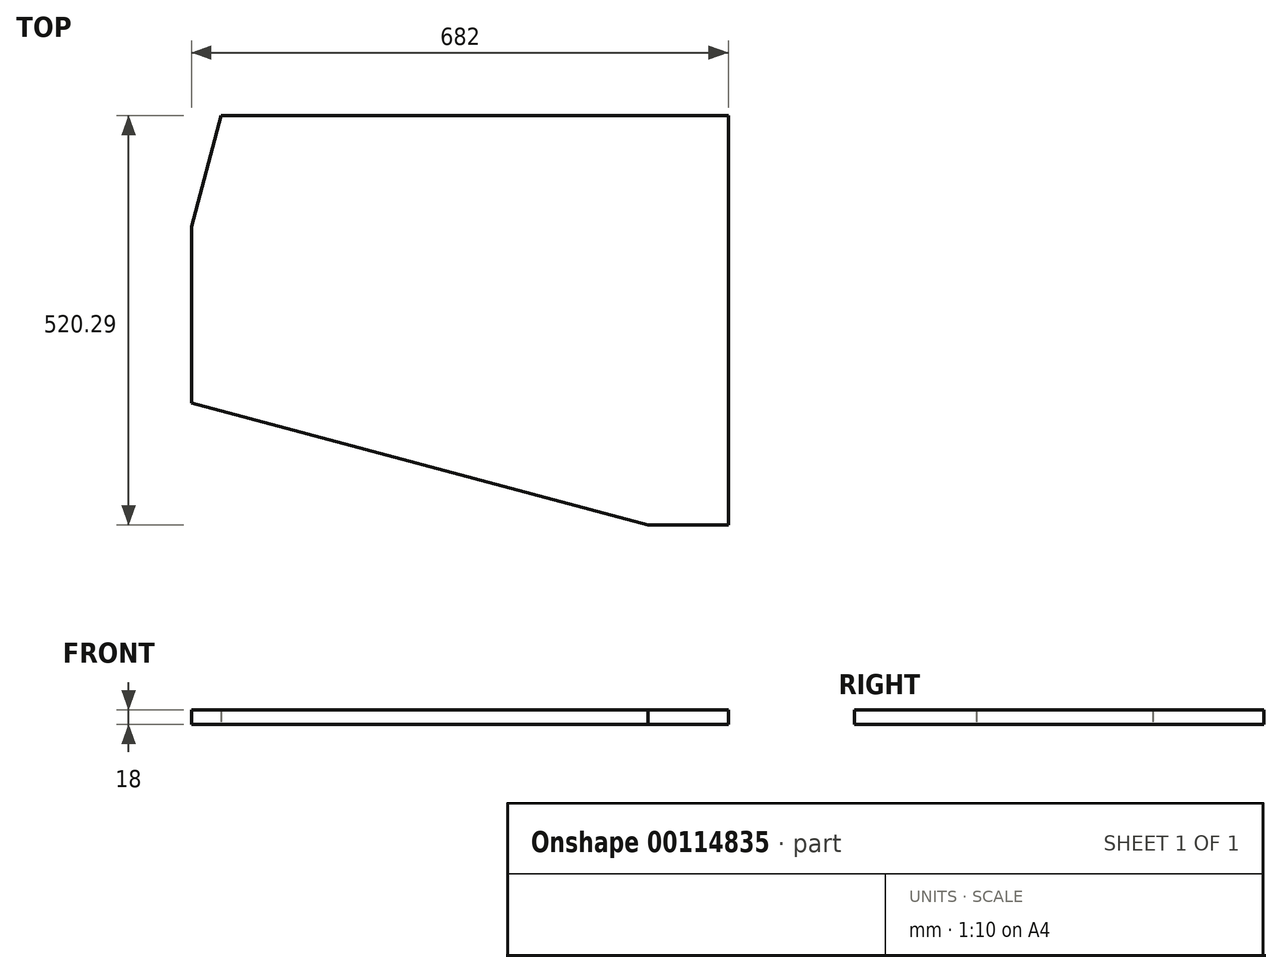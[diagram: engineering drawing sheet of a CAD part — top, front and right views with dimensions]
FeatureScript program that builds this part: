
annotation { "Feature Type Name" : "Feature", "Feature Type Description" : "" }
export const myFeature = defineFeature(function(context is Context, id is Id, definition is map)
    precondition{}
    {
        {
            var Q0;
            Q0=qCreatedBy(makeId("Top.planeOp"),FACE);
            var sketch = newSketch(context, id + "F0", { "sketchPlane" : qUnion([Q0])});
            skLineSegment(sketch, "E0.bottom", {"start": v(-1129.95, 340.55) * mm, "end": v(-447.95, 340.55) * mm, "construction": true});
            skLineSegment(sketch, "E0.top", {"start": v(-1129.95, -24.45) * mm, "end": v(-447.95, -24.45) * mm, "construction": true});
            skLineSegment(sketch, "E0.left", {"start": v(-1129.95, 340.55) * mm, "end": v(-1129.95, -24.45) * mm, "construction": true});
            skLineSegment(sketch, "E0.right", {"start": v(-447.95, 340.55) * mm, "end": v(-447.95, 100.55) * mm});
            skLineSegment(sketch, "E1", {"start": v(-1129.95, -24.45) * mm, "end": v(-1032.15, 340.55) * mm, "construction": true});
            skLineSegment(sketch, "E2", {"start": v(-447.95, -24.45) * mm, "end": v(-447.95, -179.74) * mm});
            skLineSegment(sketch, "E3", {"start": v(-447.95, 340.55) * mm, "end": v(-301.18, 340.55) * mm, "construction": true});
            skLineSegment(sketch, "E4", {"start": v(-301.18, 340.55) * mm, "end": v(-440.6, -179.74) * mm, "construction": true});
            skLineSegment(sketch, "E5", {"start": v(-1129.95, 340.55) * mm, "end": v(-1221.2, 0) * mm, "construction": true});
            skLineSegment(sketch, "E6", {"start": v(-1221.2, 0) * mm, "end": v(-1129.95, -24.45) * mm, "construction": true});
            skLineSegment(sketch, "E7", {"start": v(-1129.95, 340.55) * mm, "end": v(-1084.26, 511.05) * mm, "construction": true});
            skLineSegment(sketch, "E8", {"start": v(-447.95, 340.55) * mm, "end": v(-1084.26, 511.05) * mm, "construction": true});
            skLineSegment(sketch, "E9", {"start": v(-447.95, 340.55) * mm, "end": v(-311.02, 303.86) * mm, "construction": true});
            skPoint(sketch, "E10", {"position": v(-1048.98, 501.6) * mm});
            skLineSegment(sketch, "E11", {"start": v(-1048.98, 501.6) * mm, "end": v(-1185.92, -9.45) * mm, "construction": true});
            skPoint(sketch, "E12", {"position": v(-1092.14, 340.55) * mm});
            skPoint(sketch, "E13", {"position": v(-1129.95, 199.43) * mm});
            skLineSegment(sketch, "E14", {"start": v(-1129.95, -24.45) * mm, "end": v(-1129.95, 199.43) * mm});
            skLineSegment(sketch, "E15", {"start": v(-1092.14, 340.55) * mm, "end": v(-447.95, 340.55) * mm});
            skLineSegment(sketch, "E16", {"start": v(-550.4, -179.74) * mm, "end": v(-455.93, 172.82) * mm, "construction": true});
            skLineSegment(sketch, "E17", {"start": v(-455.93, 172.82) * mm, "end": v(-1035.48, 328.11) * mm, "construction": true});
            skLineSegment(sketch, "E18", {"start": v(-1129.95, 199.43) * mm, "end": v(-1092.14, 340.55) * mm});
            skLineSegment(sketch, "E19", {"start": v(-550.4, -179.74) * mm, "end": v(-447.95, -179.74) * mm});
            skLineSegment(sketch, "E20", {"start": v(-550.4, -179.74) * mm, "end": v(-550.4, -179.74) * mm});
            skLineSegment(sketch, "E21", {"start": v(-1129.95, -24.45) * mm, "end": v(-550.4, -179.74) * mm});
            skLineSegment(sketch, "E22", {"start": v(-550.4, -179.74) * mm, "end": v(-447.95, -207.19) * mm, "construction": true});
            skLineSegment(sketch, "E23", {"start": v(-447.95, -179.74) * mm, "end": v(-447.95, -207.19) * mm, "construction": true});
            skLineSegment(sketch, "E24", {"start": v(-1129.95, 100.55) * mm, "end": v(-447.95, 100.55) * mm, "construction": true});
            skLineSegment(sketch, "E25", {"start": v(-447.95, 100.55) * mm, "end": v(-447.95, -24.45) * mm});
            skLineSegment(sketch, "E26", {"start": v(-447.95, 340.55) * mm, "end": v(-584.88, -170.5) * mm, "construction": true});
            skLineSegment(sketch, "E27", {"start": v(-447.95, -179.74) * mm, "end": v(-440.6, -179.74) * mm, "construction": true});
            skLineSegment(sketch, "E28", {"start": v(-440.6, -179.74) * mm, "end": v(-447.95, -207.19) * mm, "construction": true});
            skSolve(sketch);
        }
        {
            var Q0;
            Q0 = qSketchRegion(id + "F0", true);
            extrude(context, id + "F1", {"entities" : qUnion([Q0]), "depth" : 18 * mm});
        }
    });
